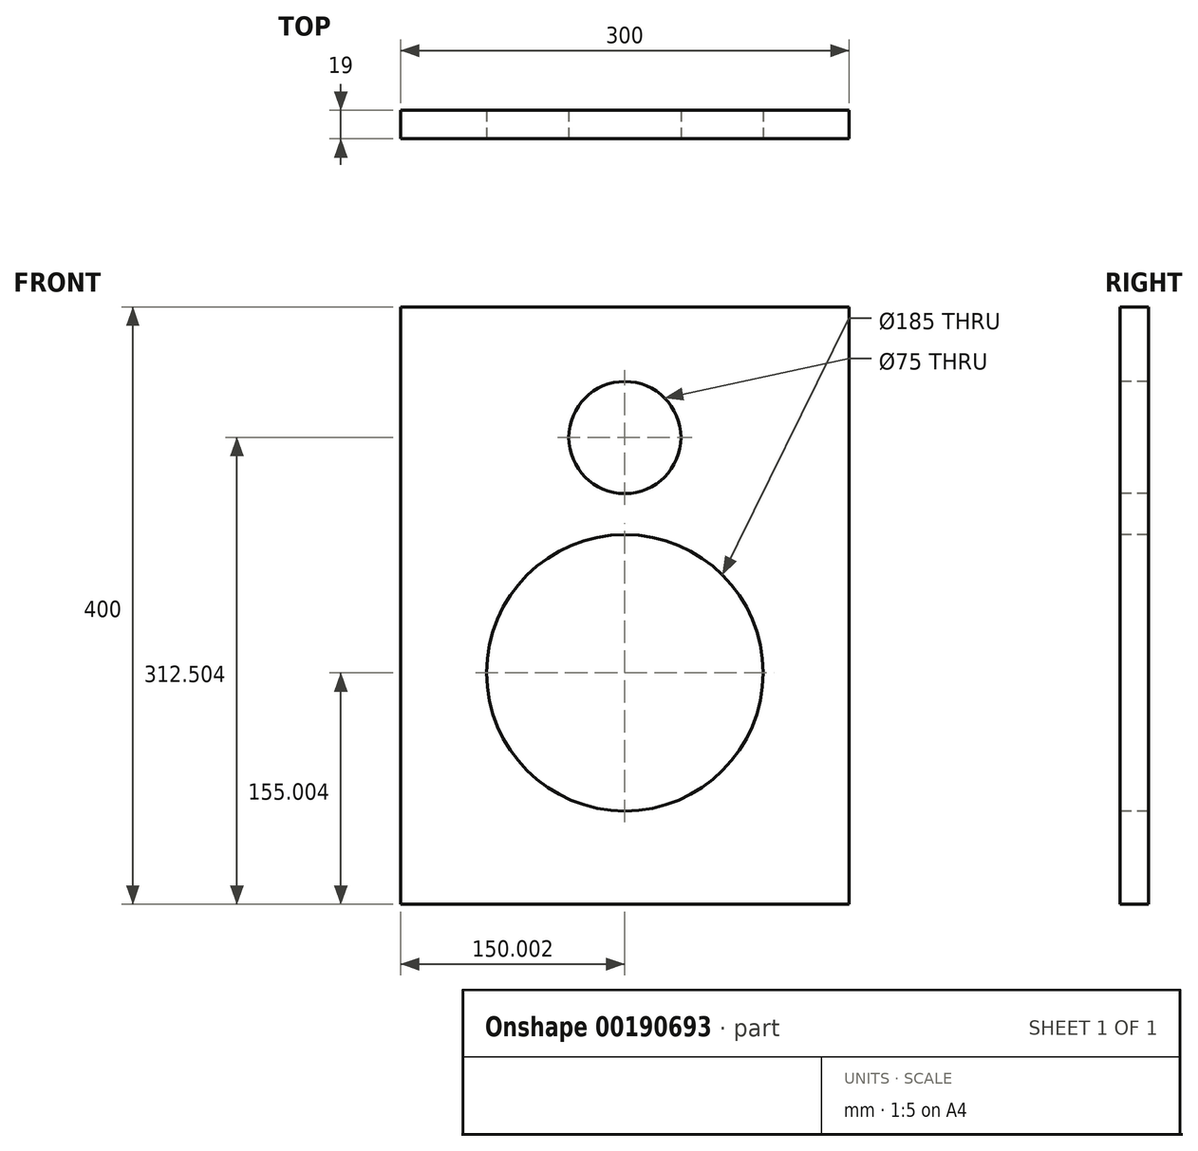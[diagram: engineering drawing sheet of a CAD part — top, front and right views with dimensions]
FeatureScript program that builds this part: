
annotation { "Feature Type Name" : "Feature", "Feature Type Description" : "" }
export const myFeature = defineFeature(function(context is Context, id is Id, definition is map)
    precondition{}
    {
        {
            var Q0;
            Q0=qCreatedBy(makeId("Front.planeOp"),FACE);
            var sketch = newSketch(context, id + "F0", { "sketchPlane" : qUnion([Q0])});
            skLineSegment(sketch, "E0.bottom", {"start": v(-159.79, 240.1) * mm, "end": v(140.21, 240.1) * mm});
            skLineSegment(sketch, "E0.top", {"start": v(-159.79, -159.9) * mm, "end": v(140.21, -159.9) * mm});
            skLineSegment(sketch, "E0.left", {"start": v(-159.79, 240.1) * mm, "end": v(-159.79, -159.9) * mm});
            skLineSegment(sketch, "E0.right", {"start": v(140.21, 240.1) * mm, "end": v(140.21, -159.9) * mm});
            skSolve(sketch);
        }
        {
            var Q0;
            Q0 = qSketchRegion(id + "F0", true);
            extrude(context, id + "F1", {"entities" : qUnion([Q0]), "depth" : 19 * mm});
        }
        {
            var Q0;
            Q0=makeQuery(id+"F1.opExtrude","CAP_FACE",FACE,{"disambiguationData":[OSD([sQuery(id+"F0.wireOp",EDGE,"E0.bottom"),sQuery(id+"F0.wireOp",EDGE,"E0.top"),sQuery(id+"F0.wireOp",EDGE,"E0.left"),sQuery(id+"F0.wireOp",EDGE,"E0.right")])],"isStart":false});
            var sketch = newSketch(context, id + "F2", { "sketchPlane" : qUnion([Q0])});
            skCircle(sketch, "E1", {"center": v(-9.79, 152.6) * mm, "radius": 37.5 * mm});
            skPoint(sketch, "E1.centerSnap0", {"position": v(-9.79, 240.1) * mm});
            skCircle(sketch, "E2", {"center": v(-9.79, -4.9) * mm, "radius": 92.5 * mm});
            skPoint(sketch, "E2.centerSnap0", {"position": v(-9.79, -159.9) * mm});
            skSolve(sketch);
        }
        {
            var Q0;
            Q0 = qSketchRegion(id + "F2", true);
            extrude(context, id + "F3", {"entities" : qUnion([Q0]), "operationType" : NewBodyOperationType.REMOVE, "oppositeDirection" : true, "depth" : 19 * mm});
        }
    });
